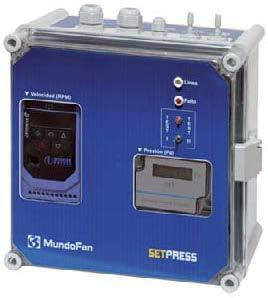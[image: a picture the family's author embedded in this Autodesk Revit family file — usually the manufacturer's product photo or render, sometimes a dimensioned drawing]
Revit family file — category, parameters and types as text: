
# Revit family: SETPRESS-15_VE10808
name_source: partatom
category: Aparatos eléctricos
revit_build: Autodesk Revit 2016 (Build: 20150220_1215(x64)
units: mm (PartAtom-declared; Revit-internal decimal feet)

## family parameters
Compartido = No
Corte con vacíos al cargar = No
Cota de conector redondo = Diámetro de uso
Mantener orientación de anotación = No
Número OmniClass = 23.80.00.00
Punto de cálculo de habitación = No
Se basa en plano de trabajo = No
Siempre vertical = Sí
Tipo de pieza = Caja de conexiones
Título OmniClass = Electric Power and Lighting

## types (1)
- SETPRESS
    Alimentación = 400Vac trifásico
    Corriente = 4,1 A
    Costo = 0 $
    Código de montaje = VE10808
    Descripción = CONTROL EFICIENCIA ENERGETICA PARA VENTILADORES
    Dimensiones máx. = 270x300x170 mm
    Fabricante = SALVADOR ESCODA
    Imagen de tipo = setpress.jpg
    Leds = linea / fallo
    Modelo = SETPRESS 1,5 kW
    Normativas = UNE-EN 12101-6
    Potencia = 1,5 kW
    Regulación = Mediante sonda analógica de presión
    Salida = 400Vac trifásico
    URL = www.salvadorescoda.com
    Visualización = frecuencia (Hz) y presión (Pa)
